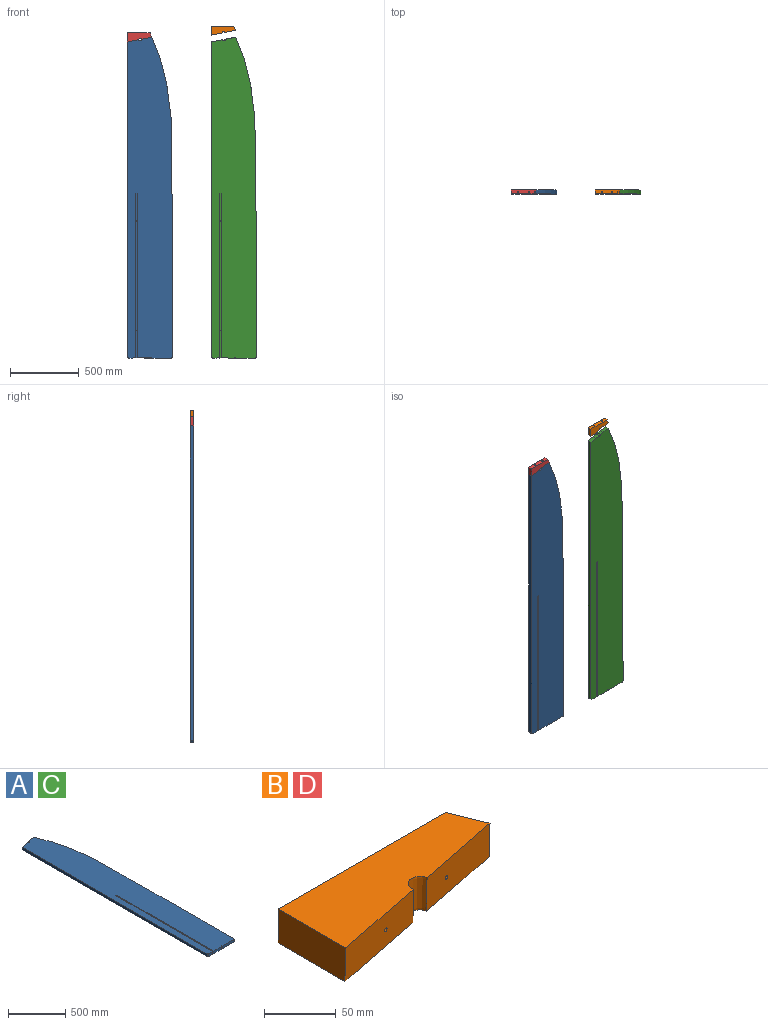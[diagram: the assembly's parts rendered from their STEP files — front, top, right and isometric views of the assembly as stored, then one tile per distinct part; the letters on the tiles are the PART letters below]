
ASSEMBLY  parts=4 mates=2
PART A: 26 faces, bbox 345.7x2355.5x44.6 mm
  f0: plane 2355.37x345.57mm, normal (0,0,1), area 712469.5mm2, adj f1,f2,f3,f7,f9,f11,f12,f13
  f1: extruded ~2327.98x152.68mm, area 68082.2mm2, adj f0,f4,f18,f21
  f2: plane 2292.72x29mm, normal (-1,0,0), area 66479.7mm2, adj f0,f4,f19,f20
  f3: extruded ~29.41x17.25mm, area 889.3mm2, adj f0,f4,f20,f21
  f4: plane 2353.23x345.62mm, normal (0,0,-1), area 712504.7mm2, adj f1,f2,f3,f12,f13,f14,f15,f16
  f5: cylinder r=2.5mm len=17mm, axis (0,0,1), area 267mm2, adj f8,f10
  f6: cylinder r=2.5mm len=17mm, axis (0,0,1), area 267mm2, adj f8,f10
  f7: plane 11.01x6.01mm, normal (0,-1,0), area 66mm2, adj f0,f9,f10,f11
  f8: plane 1199x11mm, normal (0,0,-1), area 13149.7mm2, adj f5,f6,f14,f15,f16,f17
  f9: plane 1200x6.01mm, normal (1,0,0), area 7207mm2, adj f0,f7,f10,f17
  f10: plane 1200.52x11.52mm, normal (0,0,1), area 13161.3mm2, adj f5,f6,f7,f9,f11,f17
  f11: plane 1200x5.99mm, normal (-1,0,0), area 7193mm2, adj f0,f7,f10,f17
  f12: cylinder r=5mm len=29mm, axis (0,0,1), area 455.5mm2, adj f0,f4,f13,f17
  f13: plane 141.94x29mm, normal (0,-1,0), area 4116.2mm2, adj f0,f4,f12,f18
  f14: plane 1199x6mm, normal (1,0,0), area 7194mm2, adj f4,f8,f15,f17
  f15: plane 11x6mm, normal (0,-1,0), area 66mm2, adj f4,f8,f14,f16
  f16: plane 1199x6mm, normal (-1,0,0), area 7194mm2, adj f4,f8,f15,f17
  f17: plane 158.46x29mm, normal (0,-1,0), area 4463.3mm2, adj f0,f4,f8,f9,f10,f11,f12,f14
  f18: cylinder r=10mm len=29mm, axis (0,0,1), area 456.9mm2, adj f0,f1,f4,f13
  f19: cylinder r=10mm len=29mm, axis (0,0,1), area 455.5mm2, adj f0,f2,f4,f17
  f20: plane 83.93x29.16mm, normal (-0.19,0.98,0.02), area 2469.8mm2, adj f0,f2,f3,f4,f25
  f21: plane 77.73x29.16mm, normal (-0.19,0.98,0.02), area 2282.8mm2, adj f0,f1,f3,f4,f23
  f22: cone r=0mm half-angle=59deg, axis (0,1,0), area 8.2mm2, adj f23
  f23: cylinder r=1.5mm len=48.78mm, axis (0,1,0), area 457mm2, adj f21,f22
  f24: cone r=0mm half-angle=59deg, axis (0,1,0), area 8.2mm2, adj f25
  f25: cylinder r=1.5mm len=33.88mm, axis (0,1,0), area 316.5mm2, adj f20,f24
PART B: 12 faces, bbox 180.1x68.4x31.1 mm
  f0: plane 165.06x29mm, normal (0,1,0), area 4686.2mm2, adj f1,f3,f4,f5,f9,f11
  f1: plane 179.42x67.71mm, normal (0,0,-1), area 8291.4mm2, adj f0,f2,f3,f4,f6,f7
  f2: extruded ~29.32x16.86mm, area 775.1mm2, adj f1,f5,f6,f7
  f3: plane 66.68x29mm, normal (-1,0,0), area 1924.3mm2, adj f0,f1,f5,f6
  f4: extruded ~31.32x29mm, area 973.4mm2, adj f0,f1,f5,f7
  f5: plane 180.06x68.42mm, normal (0,0,1), area 8405.3mm2, adj f0,f2,f3,f4,f6,f7
  f6: plane 83.93x29.16mm, normal (0.19,-0.98,-0.02), area 2469.8mm2, adj f1,f2,f3,f5,f10
  f7: plane 77.73x29.16mm, normal (0.19,-0.98,-0.02), area 2282.8mm2, adj f1,f2,f4,f5,f8
  f8: cylinder r=1.5mm len=39.31mm, axis (0,1,0), area 367.7mm2, adj f7,f9
  f9: cone r=1.5mm half-angle=45deg, axis (0,1,0), area 61.1mm2, adj f0,f8
  f10: cylinder r=1.5mm len=54.22mm, axis (0,1,0), area 508.2mm2, adj f6,f11
  f11: cone r=1.5mm half-angle=45deg, axis (0,1,0), area 61.1mm2, adj f0,f10
PART C: same geometry as A
PART D: same geometry as B
PLACE A rot(axis=(1,0,0),90deg) t=(305650.23,726.66,85.24)mm
PLACE B rot(axis=(1,0,0),90deg) t=(306260.62,726.66,135.24)mm
PLACE C rot(axis=(1,0,0),90deg) t=(306260.62,726.66,85.24)mm
PLACE D rot(axis=(1,0,0),90deg) t=(305650.23,726.66,85.24)mm
MATE fastened A.f0 <-> C.f0  axis (0,-1,0) through (-5074.93,697.66,85.24)mm
MATE fastened C.f0 <-> B.f5  axis (0,-1,0) through (-4784.96,697.66,2387.32)mm
